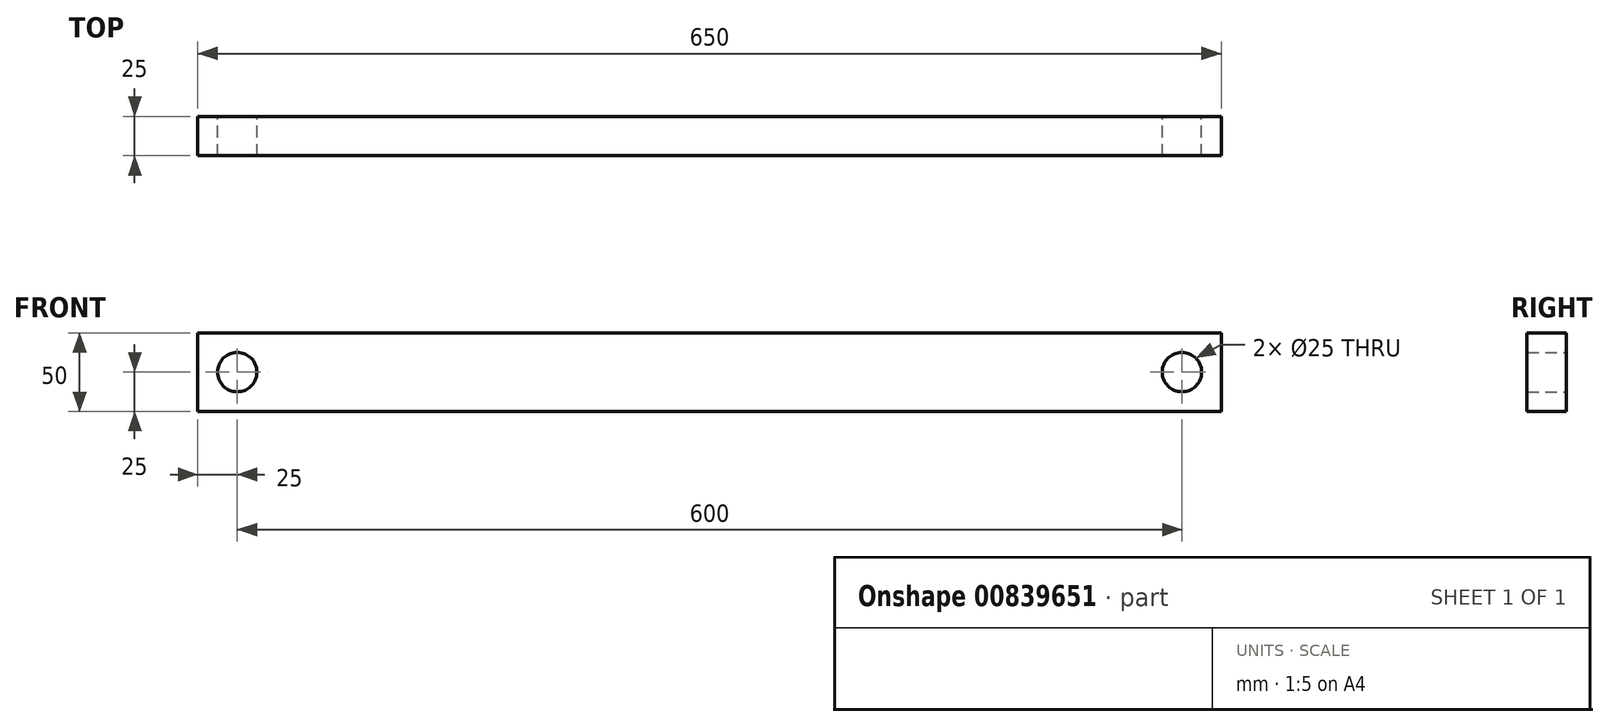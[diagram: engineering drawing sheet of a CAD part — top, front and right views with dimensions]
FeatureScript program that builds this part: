
annotation { "Feature Type Name" : "Feature", "Feature Type Description" : "" }
export const myFeature = defineFeature(function(context is Context, id is Id, definition is map)
    precondition{}
    {
        {
            var Q0;
            Q0=qCreatedBy(makeId("Front.planeOp"),FACE);
            var sketch = newSketch(context, id + "F0", { "sketchPlane" : qUnion([Q0])});
            skCircle(sketch, "E0", {"center": v(-300, 0) * mm, "radius": 12.5 * mm});
            skCircle(sketch, "E1", {"center": v(300, 0) * mm, "radius": 12.5 * mm});
            skLineSegment(sketch, "E2", {"start": v(-300, 0) * mm, "end": v(300, 0) * mm, "construction": true});
            skPoint(sketch, "E3", {"position": v(0, 0) * mm});
            skLineSegment(sketch, "E4.bottom", {"start": v(-325, 25) * mm, "end": v(325, 25) * mm});
            skLineSegment(sketch, "E4.top", {"start": v(-325, -25) * mm, "end": v(325, -25) * mm});
            skLineSegment(sketch, "E4.left", {"start": v(-325, 25) * mm, "end": v(-325, -25) * mm});
            skLineSegment(sketch, "E4.right", {"start": v(325, 25) * mm, "end": v(325, -25) * mm});
            skLineSegment(sketch, "E5", {"start": v(300, 0) * mm, "end": v(325, 25) * mm, "construction": true});
            skLineSegment(sketch, "E6", {"start": v(300, 0) * mm, "end": v(325, -25) * mm, "construction": true});
            skLineSegment(sketch, "E7", {"start": v(-300, 0) * mm, "end": v(-325, 25) * mm, "construction": true});
            skLineSegment(sketch, "E8", {"start": v(-300, 0) * mm, "end": v(-325, -25) * mm, "construction": true});
            skSolve(sketch);
        }
        {
            var Q0;
            Q0=makeQuery(id+"F0.imprint","IMPRINT",FACE,{"disambiguationData":[TD([[makeQuery(id+"F0.imprint","IMPRINT",EDGE,{"derivedFrom":sQuery(id+"F0.wireOp",EDGE,"E0")}),-1.0]])]});
            extrude(context, id + "F1", {"entities" : qUnion([Q0]), "depth" : 25 * mm, "offsetDistance" : 25 * mm});
        }
    });
